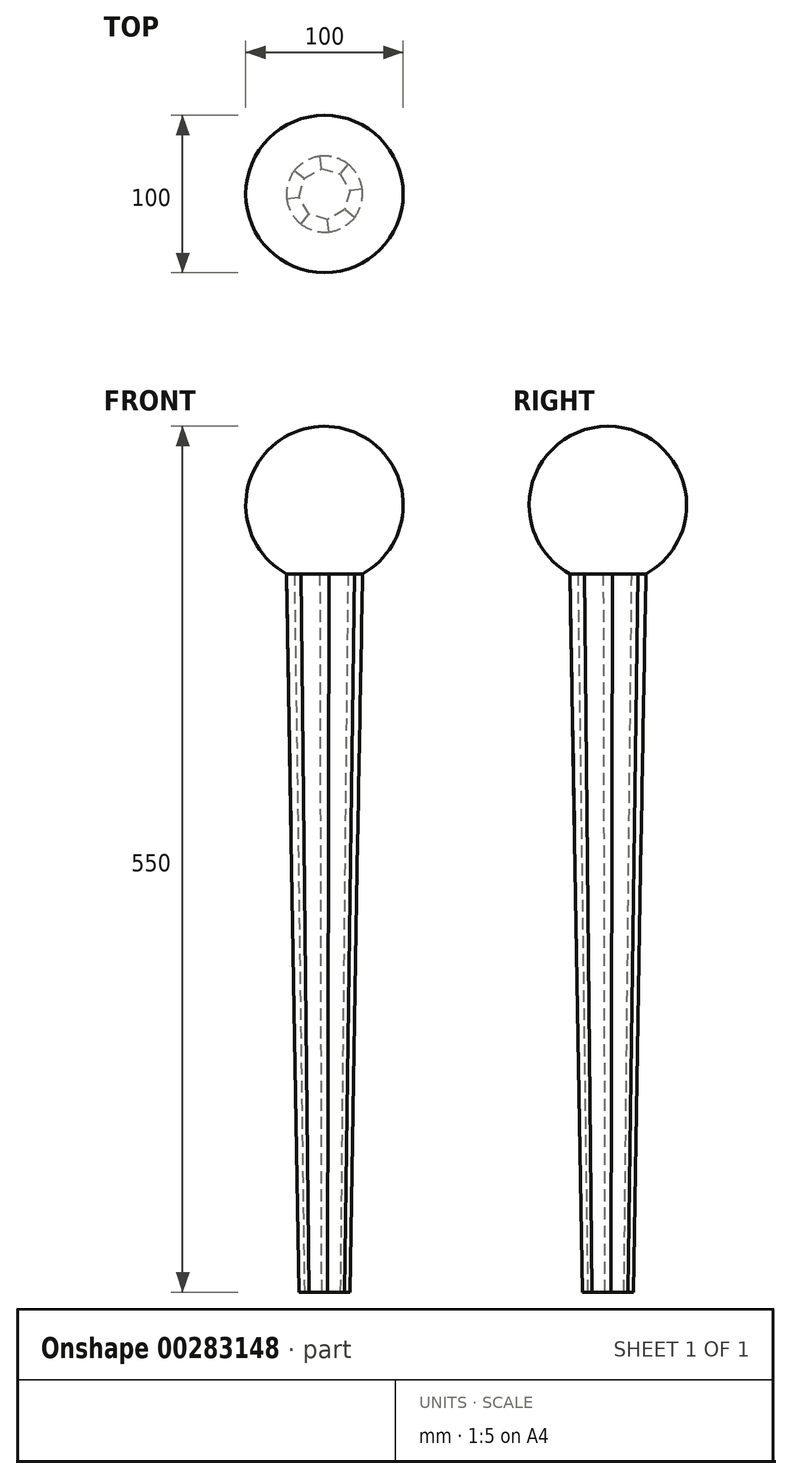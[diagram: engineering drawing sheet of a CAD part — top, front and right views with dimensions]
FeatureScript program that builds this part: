
annotation { "Feature Type Name" : "Feature", "Feature Type Description" : "" }
export const myFeature = defineFeature(function(context is Context, id is Id, definition is map)
    precondition{}
    {
        {
            var Q0;
            Q0=qCreatedBy(makeId("Top.planeOp"),FACE);
            cPlane(context, id + "F0", {"entities" : qUnion([Q0]), "cplaneType" : CPlaneType.OFFSET, "offset" : 500 * mm, "width" : 150 * mm, "height" : 150 * mm});
        }
        {
            var Q0;
            Q0=qCreatedBy(makeId("Top.planeOp"),FACE);
            var sketch = newSketch(context, id + "F1", { "sketchPlane" : qUnion([Q0])});
            skCircle(sketch, "E0.cCircle", {"center": v(0, 0) * mm, "radius": 15 * mm, "construction": true});
            skLineSegment(sketch, "E0.0", {"start": v(12.82, -9.97) * mm, "end": v(2.02, -16.11) * mm});
            skLineSegment(sketch, "E0.1", {"start": v(2.02, -16.11) * mm, "end": v(-9.97, -12.82) * mm});
            skLineSegment(sketch, "E0.2", {"start": v(-9.97, -12.82) * mm, "end": v(-16.11, -2.02) * mm});
            skLineSegment(sketch, "E0.3", {"start": v(-16.11, -2.02) * mm, "end": v(-12.82, 9.97) * mm});
            skLineSegment(sketch, "E0.4", {"start": v(-12.82, 9.97) * mm, "end": v(-2.02, 16.11) * mm});
            skLineSegment(sketch, "E0.5", {"start": v(-2.02, 16.11) * mm, "end": v(9.97, 12.82) * mm});
            skLineSegment(sketch, "E0.6", {"start": v(9.97, 12.82) * mm, "end": v(16.11, 2.02) * mm});
            skLineSegment(sketch, "E0.7", {"start": v(16.11, 2.02) * mm, "end": v(12.82, -9.97) * mm});
            skPoint(sketch, "E0.0.midPoint", {"position": v(7.42, -13.04) * mm});
            skSolve(sketch);
        }
        {
            var Q0;
            Q0=qCreatedBy(id+"F0.planeOp",FACE);
            var sketch = newSketch(context, id + "F2", { "sketchPlane" : qUnion([Q0])});
            skCircle(sketch, "E1", {"center": v(0, 0) * mm, "radius": 25 * mm});
            skSolve(sketch);
        }
        {
            var Q0;
            Q0=makeQuery(id+"F2.imprint","IMPRINT",FACE,{"disambiguationData":[TD([[makeQuery(id+"F2.imprint","IMPRINT",EDGE,{"derivedFrom":sQuery(id+"F2.wireOp",EDGE,"E1")}),1.0]])]});
            var Q1;
            Q1=makeQuery(id+"F1.imprint","IMPRINT",FACE,{"disambiguationData":[TD([[makeQuery(id+"F1.imprint","IMPRINT",EDGE,{"derivedFrom":sQuery(id+"F1.wireOp",EDGE,"E0.0")}),-1.0]])]});
            loft(context, id + "F3", {"sheetProfilesArray" : [{ "sheetProfileEntities" : qUnion([Q0]) }, { "sheetProfileEntities" : qUnion([Q1]) }]});
        }
        {
            var Q0;
            Q0=qCreatedBy(id+"F0.planeOp",FACE);
            cPlane(context, id + "F4", {"entities" : qUnion([Q0]), "cplaneType" : CPlaneType.OFFSET, "offset" : 0 * mm, "width" : 150 * mm, "height" : 150 * mm});
        }
        {
            var Q0;
            Q0=qCreatedBy(id+"F4.planeOp",FACE);
            var sketch = newSketch(context, id + "F5", { "sketchPlane" : qUnion([Q0])});
            skArc(sketch, "E2", {"start": v(0, 50) * mm, "mid": v(-50, 0) * mm, "end": v(0, -50) * mm});
            skLineSegment(sketch, "E3", {"start": v(0, 50) * mm, "end": v(0, -50) * mm});
            skSolve(sketch);
        }
        {
            var Q0;
            Q0=makeQuery(id+"F5.imprint","IMPRINT",FACE,{"disambiguationData":[TD([[makeQuery(id+"F5.imprint","IMPRINT",EDGE,{"derivedFrom":sQuery(id+"F5.wireOp",EDGE,"E2")}),1.0]])]});
            var Q1;
            Q1=sQuery(id+"F5.wireOp",EDGE,"E3");
            revolve(context, id + "F6", {"operationType" : NewBodyOperationType.ADD, "entities" : qUnion([Q0]), "axis" : qUnion([Q1]), "revolveType" : RevolveType.FULL});
        }
    });
